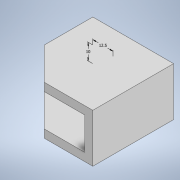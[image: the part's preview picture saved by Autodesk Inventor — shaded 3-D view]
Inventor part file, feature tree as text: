
AUTODESK INVENTOR PART (.ipt)
format: ipt  version: 2022 (Build 260153000, 153)  size: 228,352 bytes
history: native  units: mm
features: sketch x10, extrude x6, projected_geometry x4, fillet x3, hole x2
ambient origin geometry x8: Origin, YZ Plane, XZ Plane, XY Plane, X Axis, Y Axis, Z Axis, Center Point
bodies: Solid1 (feature_tree)
feature tree (25):
  extrude  "Extrusion1"  Depth=20.0mm
  extrude  "Extrusion2"  Depth=10.0mm
  sketch  "Sketch4"  dims[d4=20.0mm d5=0.0mm d6=5.0mm]
  sketch  "Sketch5"  dims[d7=5.0mm d8=135.0deg]
  extrude  "Extrusion4"  Depth=5.0mm
  extrude  "Extrusion5"  TaperAngle=135.0deg  [1 undecoded]
  extrude  "Extrusion6"  Depth=30.0mm
  extrude  "Extrusion7"  Depth=5.0mm TaperAngle=0.0deg
  sketch  "Sketch13"  dims[d33=10.0mm]
  hole  "Hole1"  [1 undecoded]
  hole  "Hole2"  [1 undecoded]
  fillet  "Fillet1"  Radius=5.0mm
  fillet  "Fillet2"  Radius=5.0mm
  fillet  "Fillet3"  Radius=12.5mm
  sketch  "Sketch1"  dims[d0=20.0mm d1=20.0mm]
  sketch  "Sketch2"  dims[d2=10.0mm d3=10.0mm]
  sketch  "Sketch6"  dims[d9=30.0mm d10=30.0mm]
  sketch  "Sketch7"  dims[d11=50.0mm d12=5.0mm d13=0.0mm]
  projected_geometry  "Projected Loop1"
  projected_geometry  "Projected Loop2"
  sketch  "Sketch8"  dims[d18=5.0mm d21=5.0mm]
  sketch  "Sketch9"  dims[d22=20.0mm d23=0.0mm d24=5.0mm d25=0.0mm d26=5.0mm d27=0.0mm d28=5.0mm d29=0.0mm d32=12.5mm]
  projected_geometry  "Projected Loop4"
  sketch  "Sketch14"  dims[d34=12.5mm d35=10.0mm d36=3.4mm d37=6.0mm d38=6.5mm d39=3.0mm d40=90.0deg d41=8.0mm d42=20.594885mm d43=3.4mm d44=6.0mm d45=6.5mm d46=3.0mm d47=90.0deg d48=8.0mm d49=20.594885mm d50=10.0mm d51=5.0mm d52=2.0mm]
  projected_geometry  "Projected Loop5"
note: 3 required parameter values undecoded (feature->parameter linkage not recoverable at this tier; creation-order binding heuristic only, values carry confidence <= 0.55)
